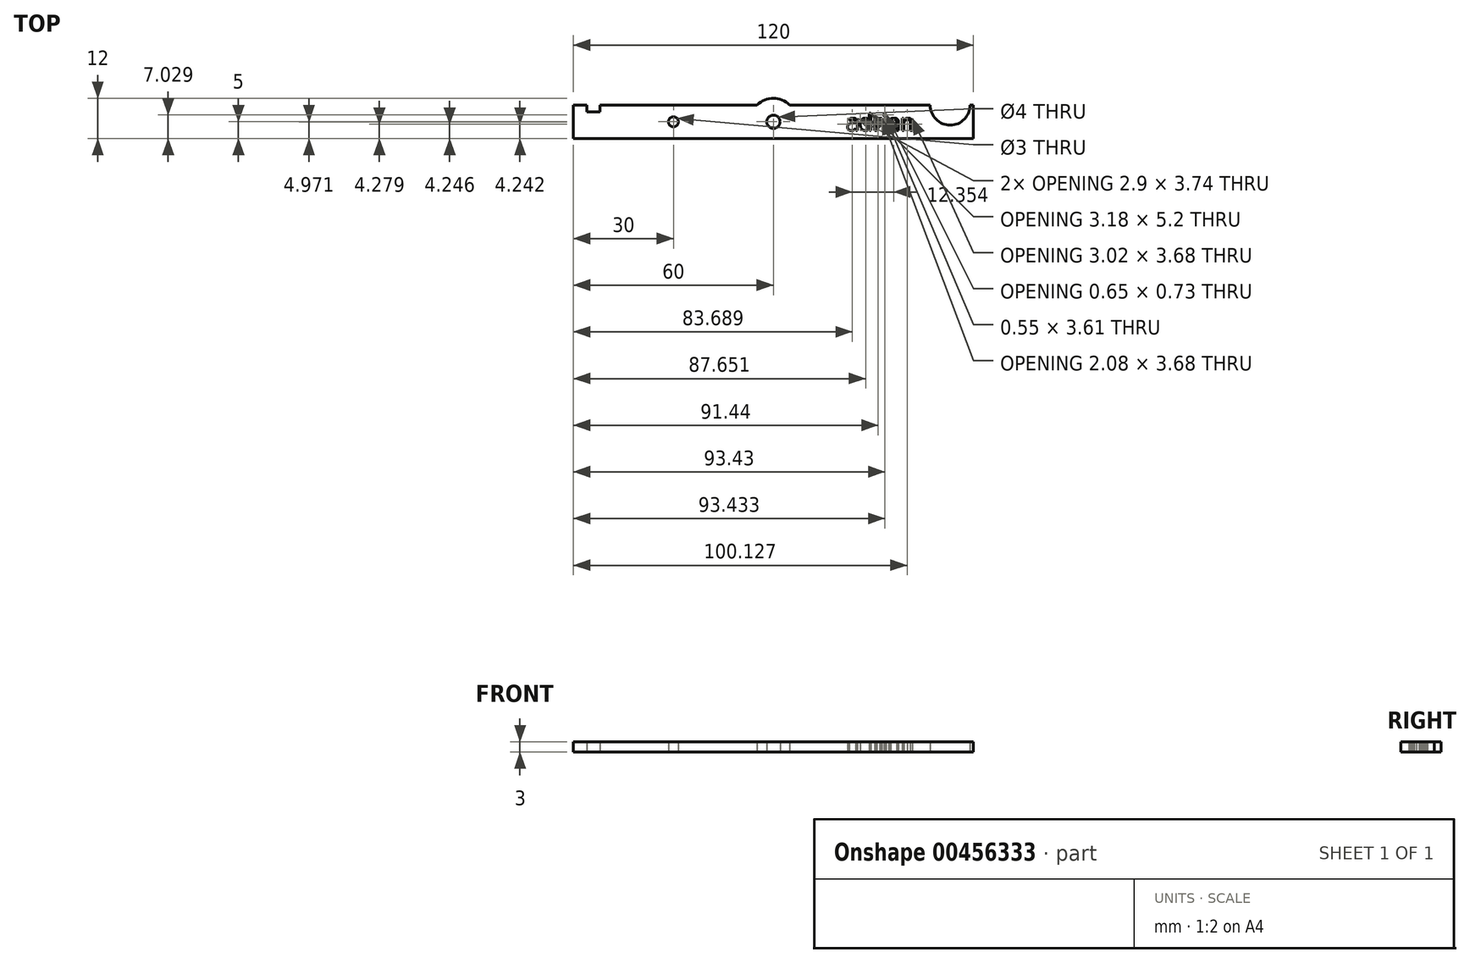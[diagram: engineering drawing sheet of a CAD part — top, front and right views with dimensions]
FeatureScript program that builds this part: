
annotation { "Feature Type Name" : "Feature", "Feature Type Description" : "" }
export const myFeature = defineFeature(function(context is Context, id is Id, definition is map)
    precondition{}
    {
        {
            var Q0;
            Q0=qCreatedBy(makeId("Top.planeOp"),FACE);
            var sketch = newSketch(context, id + "F0", { "sketchPlane" : qUnion([Q0])});
            skLineSegment(sketch, "E0.bottom", {"start": v(-60, -5) * mm, "end": v(60, -5) * mm});
            skLineSegment(sketch, "E0.top", {"start": v(-60, 5) * mm, "end": v(60, 5) * mm});
            skLineSegment(sketch, "E0.left", {"start": v(-60, -5) * mm, "end": v(-60, 5) * mm});
            skLineSegment(sketch, "E0.right", {"start": v(60, -5) * mm, "end": v(60, 5) * mm});
            skPoint(sketch, "E0.middle", {"position": v(0, 0) * mm});
            skLineSegment(sketch, "E1.bottom", {"start": v(-52, 5) * mm, "end": v(-56, 5) * mm});
            skLineSegment(sketch, "E1.top", {"start": v(-52, 3) * mm, "end": v(-56, 3) * mm});
            skLineSegment(sketch, "E1.left", {"start": v(-52, 5) * mm, "end": v(-52, 3) * mm});
            skLineSegment(sketch, "E1.right", {"start": v(-56, 5) * mm, "end": v(-56, 3) * mm});
            skCircle(sketch, "E2", {"center": v(0, 0) * mm, "radius": 2 * mm});
            skCircle(sketch, "E3", {"center": v(0, 0) * mm, "radius": 7 * mm});
            skCircle(sketch, "E4", {"center": v(-30, 0) * mm, "radius": 1.5 * mm});
            skCircle(sketch, "E5", {"center": v(53, 5) * mm, "radius": 6 * mm});
            skText(sketch, "E6", { "text": "adrian\n", "fontName": "OpenSans-Regular.ttf"});
            const initialGuessF0  = {"E6": [0.02193, -0.00256, 1, 0, 0.00486]};
            skSetInitialGuess(sketch, initialGuessF0);
            skSolve(sketch);
        }
        {
            var Q0;
            {var subQ0=sQuery(id+"F0.wireOp",EDGE,"E0.left");Q0=makeQuery(id+"F0.imprint","IMPRINT",FACE,{"disambiguationData":[TD([[makeQuery(id+"F0.imprint","IMPRINT",EDGE,{"derivedFrom":subQ0}),-1.0]])]});}
            var Q1;
            Q1=makeQuery(id+"F0.imprint","IMPRINT",FACE,{"disambiguationData":[TD([[makeQuery(id+"F0.imprint","IMPRINT",EDGE,{"derivedFrom":sQuery(id+"F0.wireOp",EDGE,"E2")}),-1.0]])]});
            var Q2;
            {var subQ0=sQuery(id+"F0.wireOp",EDGE,"E3");var subQ1=sQuery(id+"F0.wireOp",EDGE,"E0.top");var subQ2=makeQuery(id+"F0.imprint","INTERSECT",VERTEX,{"disambiguationData":[OD(0.0)],"derivedFrom":[subQ1,subQ0]});Q2=makeQuery(id+"F0.imprint","IMPRINT",FACE,{"disambiguationData":[TD([[makeQuery(id+"F0.imprint","IMPRINT",EDGE,{"disambiguationData":[TD([[subQ2,-1.0]])],"derivedFrom":subQ1}),1.0]])]});}
            var Q3;
            {var subQ0=sQuery(id+"F0.wireOp",EDGE,"E3");var subQ1=sQuery(id+"F0.wireOp",EDGE,"E0.bottom");var subQ2=makeQuery(id+"F0.imprint","INTERSECT",VERTEX,{"disambiguationData":[OD(0.0)],"derivedFrom":[subQ1,subQ0]});Q3=makeQuery(id+"F0.imprint","IMPRINT",FACE,{"disambiguationData":[TD([[makeQuery(id+"F0.imprint","IMPRINT",EDGE,{"disambiguationData":[TD([[subQ2,-1.0]])],"derivedFrom":subQ1}),-1.0]])]});}
            var Q4;
            {var subQ0=sQuery(id+"F0.wireOp",EDGE,"E0.right");Q4=makeQuery(id+"F0.imprint","IMPRINT",FACE,{"disambiguationData":[TD([[makeQuery(id+"F0.imprint","IMPRINT",EDGE,{"derivedFrom":subQ0}),1.0]])]});}
            extrude(context, id + "F1", {"entities" : qUnion([Q0, Q1, Q2, Q3, Q4]), "depth" : 3 * mm});
        }
    });
